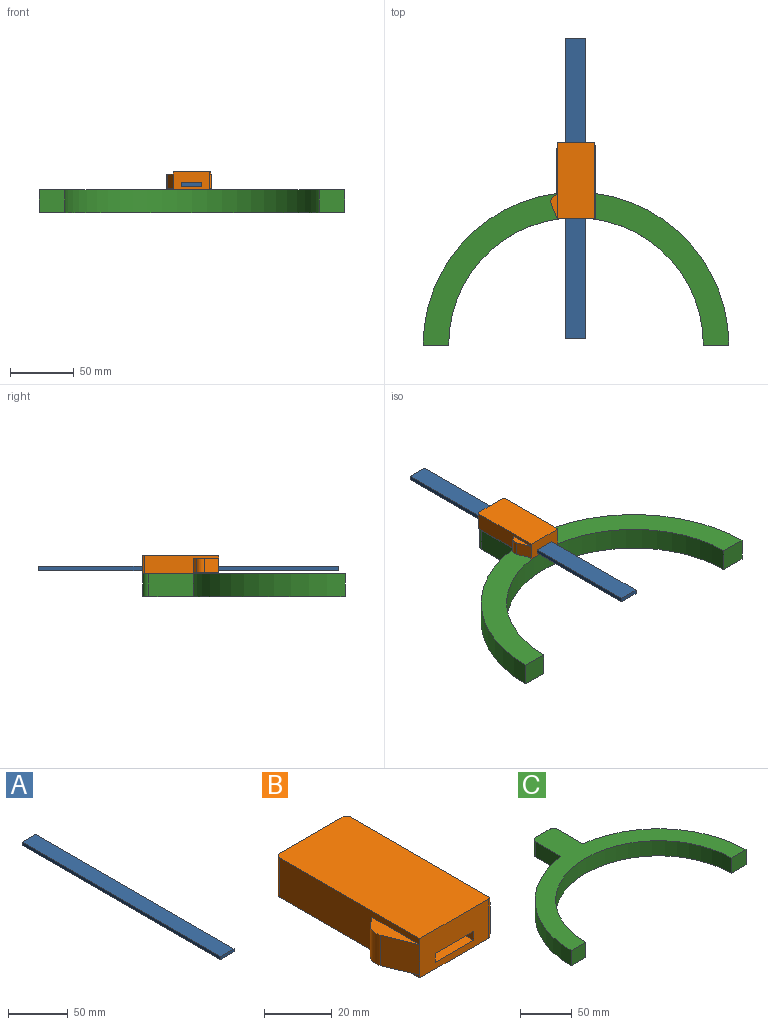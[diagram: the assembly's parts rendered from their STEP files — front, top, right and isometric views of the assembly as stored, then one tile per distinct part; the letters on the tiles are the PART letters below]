
ASSEMBLY  parts=3 mates=2
PART A: 6 faces, bbox 16x235x3.2 mm
  f0: plane 235x3.2mm, normal (-1,0,0), area 752mm2, adj f1,f3,f4,f5
  f1: plane 16x3.2mm, normal (0,-1,0), area 51.2mm2, adj f0,f2,f4,f5
  f2: plane 235x3.2mm, normal (1,0,0), area 752mm2, adj f1,f3,f4,f5
  f3: plane 16x3.2mm, normal (0,1,0), area 51.2mm2, adj f0,f2,f4,f5
  f4: plane 235x16mm, normal (0,0,1), area 3760mm2, adj f0,f1,f2,f3
  f5: plane 235x16mm, normal (0,0,-1), area 3760mm2, adj f0,f1,f2,f3
PART B: 27 faces, bbox 35.2x60x14.2 mm
  f0: plane 58.5x14.2mm, normal (-1,0,0), area 610.7mm2, adj f1,f4,f5,f10,f13,f14,f25
  f1: plane 28.7x14.2mm, normal (0,-1,0), area 356.3mm2, adj f0,f4,f5,f6,f7,f8,f9,f12
  f2: plane 58.27x14.2mm, normal (1,0,0), area 412mm2, adj f4,f5,f15,f17,f18,f19,f21,f22
  f3: plane 26.5x14.2mm, normal (0,1,0), area 325.1mm2, adj f4,f5,f6,f7,f8,f9,f24,f25
  f4: plane 60x29.5mm, normal (0,0,1), area 1769mm2, adj f0,f1,f2,f3,f24,f25,f26
  f5: plane 60x29.5mm, normal (0,0,-1), area 1769mm2, adj f0,f1,f2,f3,f24,f25,f26
  f6: plane 60x3.2mm, normal (1,0,0), area 192mm2, adj f1,f3,f7,f9
  f7: plane 60x16mm, normal (0,0,1), area 960mm2, adj f1,f3,f6,f8
  f8: plane 60x3.2mm, normal (-1,0,0), area 192mm2, adj f1,f3,f7,f9
  f9: plane 60x16mm, normal (0,0,-1), area 960mm2, adj f1,f3,f6,f8
  f10: plane 11x3.21mm, normal (-0.64,0.77,0), area 46mm2, adj f0,f11,f13,f14
  f11: cylinder r=5mm len=11mm, axis (0,0,-1), area 69.1mm2, adj f10,f12,f13,f14
  f12: plane 11.63x11mm, normal (-0.93,-0.37,0), area 137.8mm2, adj f1,f11,f13,f14
  f13: plane 20x5.01mm, normal (0,0,1), area 57.5mm2, adj f0,f10,f11,f12
  f14: plane 20x5.01mm, normal (0,0,-1), area 57.5mm2, adj f0,f10,f11,f12
  f15: plane 11x0.7mm, normal (0,-1,0), area 7.7mm2, adj f2,f16,f18,f19
  f16: plane 19x11mm, normal (1,0,0), area 209mm2, adj f15,f17,f18,f19
  f17: plane 11x0.7mm, normal (0,1,0), area 7.7mm2, adj f2,f16,f18,f19
  f18: plane 19x0.7mm, normal (0,0,1), area 13.3mm2, adj f2,f15,f16,f17
  f19: plane 19x0.7mm, normal (0,0,-1), area 13.3mm2, adj f2,f15,f16,f17
  f20: plane 17.5x11mm, normal (1,0,0), area 192.5mm2, adj f21,f22,f23,f26
  f21: plane 11x0.7mm, normal (0,1,0), area 7.7mm2, adj f2,f20,f22,f23
  f22: plane 18.77x0.7mm, normal (0,0,1), area 12.9mm2, adj f2,f20,f21,f26
  f23: plane 18.77x0.7mm, normal (0,0,-1), area 12.9mm2, adj f2,f20,f21,f26
  f24: cylinder r=1.5mm len=14.2mm, axis (0,0,-1), area 33.5mm2, adj f2,f3,f4,f5
  f25: cylinder r=1.5mm len=14.2mm, axis (0,0,-1), area 33.5mm2, adj f0,f3,f4,f5
  f26: cylinder r=1.5mm len=14.2mm, axis (0,0,1), area 28.6mm2, adj f1,f2,f4,f5,f20,f22,f23
PART C: 12 faces, bbox 240x159.1x18 mm
  f0: plane 35x18mm, normal (-1,0,0), area 630mm2, adj f1,f9,f10,f11
  f1: cylinder r=120mm len=119.06mm, axis (0,0,-1), area 3122.2mm2, adj f0,f2,f10,f11
  f2: plane 20x18mm, normal (0,-1,0), area 360mm2, adj f1,f3,f10,f11
  f3: cylinder r=100mm len=200mm, axis (0,0,-1), area 5654.9mm2, adj f2,f4,f10,f11
  f4: plane 20x18mm, normal (0,-1,0), area 360mm2, adj f3,f5,f10,f11
  f5: cylinder r=120mm len=119.06mm, axis (0,0,-1), area 3122.2mm2, adj f4,f6,f10,f11
  f6: plane 35x18mm, normal (1,0,0), area 630mm2, adj f5,f7,f10,f11
  f7: cylinder r=5mm len=18mm, axis (0,0,-1), area 141.4mm2, adj f6,f8,f10,f11
  f8: plane 20x18mm, normal (0,1,0), area 360mm2, adj f7,f9,f10,f11
  f9: cylinder r=5mm len=18mm, axis (0,0,-1), area 141.4mm2, adj f0,f8,f10,f11
  f10: plane 240x159.06mm, normal (0,0,1), area 8081.9mm2, adj f0,f1,f2,f3,f4,f5,f6,f7
  f11: plane 240x159.06mm, normal (0,0,-1), area 8081.9mm2, adj f0,f1,f2,f3,f4,f5,f6,f7
PLACE A t=(-8.25,5.41,20.4)mm
PLACE B t=(-14.75,99.06,18)mm
PLACE C at identity fixed
MATE fastened C.f10 <-> B.f5  axis (0,0,1) through (0,159.06,18)mm
MATE slider B.f1 <-> A.f1  axis (0,-1,0) through (-0.25,99.06,23.6)mm
